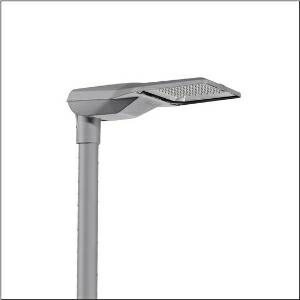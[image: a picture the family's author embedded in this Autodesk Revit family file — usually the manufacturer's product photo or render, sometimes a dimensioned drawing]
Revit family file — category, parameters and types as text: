
# Revit family: streetlight_sl_21_iq_midi___st0_8a_5xe3c41g08mb_fe6c
name_source: partatom
category: Lighting Fixtures
units: mm (PartAtom-declared; Revit-internal decimal feet)

## family parameters
Cut with Voids When Loaded = No
Host = Face
Light Source = No
Part Type = Normal
Room Calculation Point = No
Round Connector Dimension = Use Diameter
Shared = No

## types (1)
- --- (1 x LED, 20360 lm, 146.7 W, 4000K)
    Apparent Load = 147 VA
    CIE Flux Codes = 38 75 97 100 100
    Color Rendering = 70
    Color Temperature = 4000K
    Default Elevation = 1800 mm
    Description = Streetlight SL 21 iQ midi, mast luminaire, primary light control with lens, of PMMA, primary optical cover: cover, of toughened safety glass, transparent, light distribution: ST0.8a, light emission: direct distribution, primary light characteristic: asymmetric, installation type: post-top, side-entry, LED, High Power LED, rated luminous flux: 20.360lm, luminous efficacy: 139lm/W, light colour: 740, colour temperature: 4000K, control gear: iQ Street-Remote, control: Street-Remote, Auto-Match, Temp-Guard, Lumen-Switch, Night-Set, Smart-Wire, Light-Fading, Desk-Remote (wireless, voltage-free reading and setting of iQ features in the workshop via application-optimized NFC function/RFID function), optimised constant luminous flux control (CLO 2.0), pre-setting: linear dimming characteristic, mains connection: 230..240V, AC, 50/60Hz, start of lifetime: 147W, end of service life: 161W, reduction: 62W, luminaire housing, of diecast aluminium, powder-coated, Siteco® metallic grey (DB 702S), corrosivity category C5 mid according to DIN EN ISO 12944, please order mast flange separately, inclination adjustable: 0°, 5°, 10°, 15°, sealing non-destructively replaceable, multi-level sealing system, length: 644mm, width: 335mm, height: 110mm, mast flange for spigot size: 42mm (side-entry): 5XC10008XM4, 60/48mm (side-entry/post-top): 5XC10108XM2, 76/60mm (side-entry/post-top): 5XC10108XM1, mounting height: 4..8m, protection rating (complete): IP66, insulation class (complete): insulation class II (safety insulation), certification: CE, ENEC, ENEC+, VDE, impact resistance: IK10, permissible operating ambient temperature for outdoor applications: -40..+50°C, standard-compliant lighting for roads and squares, packaging unit: 1 piece

Light Distribution: ST0.8a
    Height = 111 mm
    Lamp = 1 x LED
    Lamp Light Flux = 20360 lm
    Lamp Power = 146.7 W
    Lamp count = 1
    Length = 644 mm
    Luminous efficacy = 139 lm/W
    Manufacturer = Siteco
    ModVariant = No
    Model = 5XE3C41G08MB
    Number of Poles = 1
    OnlyDefault = Yes
    Power Factor = 1
    Product Name = Streetlight SL 21 iQ midi | ST0.8a
    Product group = mast luminaire | pylon top
    ProductGroupID = 6100
    Protection Class = Protection class II
    Protection Degree = IP 66
    RLX_Detail_Level = 1
    RLX_Emergency_Light_Flux = 0 lm
    RLX_Emergency_Type = 0
    RLX_Emergency_Type_DB = No
    RlxData = <blob elided: 26977 chars, md5=b58d419d>
    Socket = socket
    Standby Power = 0 W
    System Light Flux = 20360 lm
    System Power = 147 W
    Type Comments = factory setting: luminous flux: 100 % | dim-lin: 254 | 753 mA
    Type Image = l_1004298.jpg
    URL = http://relux.com
    VarID = @adj_207443
    Voltage = 0 V
    Weight = 0.00 kg
    Width = 336 mm

## geometry (parser evidence)
native form markers: Blend x4, Sweep x11
no freeform markers — native parametric forms only
